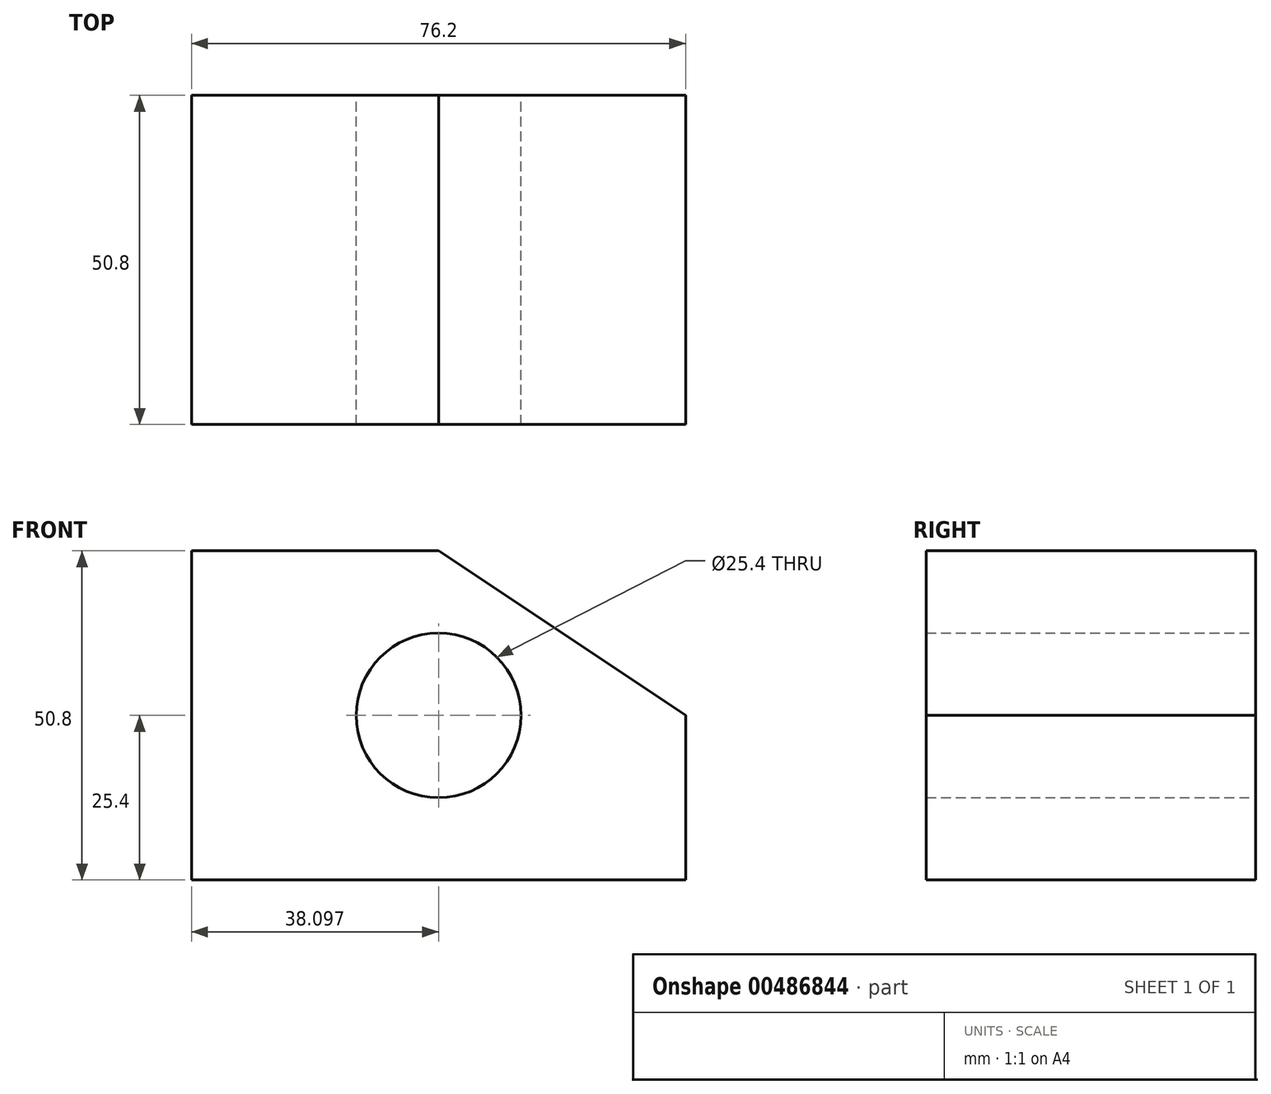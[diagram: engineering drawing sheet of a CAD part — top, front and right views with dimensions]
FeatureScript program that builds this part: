
annotation { "Feature Type Name" : "Feature", "Feature Type Description" : "" }
export const myFeature = defineFeature(function(context is Context, id is Id, definition is map)
    precondition{}
    {
        {
            var Q0;
            Q0=qCreatedBy(makeId("Front.planeOp"),FACE);
            var sketch = newSketch(context, id + "F0", { "sketchPlane" : qUnion([Q0])});
            skLineSegment(sketch, "E0.bottom", {"start": v(2.18, 0) * mm, "end": v(78.38, 0) * mm});
            skLineSegment(sketch, "E0.top", {"start": v(2.18, 50.8) * mm, "end": v(40.28, 50.8) * mm});
            skLineSegment(sketch, "E0.left", {"start": v(2.18, 0) * mm, "end": v(2.18, 50.8) * mm});
            skLineSegment(sketch, "E0.right", {"start": v(78.38, 0) * mm, "end": v(78.38, 25.4) * mm});
            skCircle(sketch, "E1", {"center": v(40.28, 25.4) * mm, "radius": 12.7 * mm});
            skLineSegment(sketch, "E2", {"start": v(78.38, 25.4) * mm, "end": v(40.28, 50.8) * mm});
            skSolve(sketch);
        }
        {
            var Q0;
            Q0=makeQuery(id+"F0.imprint","IMPRINT",FACE,{"disambiguationData":[TD([[makeQuery(id+"F0.imprint","IMPRINT",EDGE,{"derivedFrom":sQuery(id+"F0.wireOp",EDGE,"E0.bottom")}),1.0]])]});
            extrude(context, id + "F1", {"entities" : qUnion([Q0]), "depth" : 50.8 * mm});
        }
    });
